# Revit family: 13961 Информационный указатель «Линк» Хоббика
name_source: partatom
category: Антураж
revit_build: Autodesk Revit 2018 (Build: 20180423_1000(x64)
units: mm (PartAtom-declared; Revit-internal decimal feet)

## family parameters
Всегда вертикально = Да
Источник визуального образа = Геометрия семейства
На основе рабочей плоскости = Нет
Общий = Нет
При загрузке вырезать с полостями = Нет
Точка расчета площади = Нет

## types (2) — shared parameters
URL = https://hobbyka.ru
Артикул товара = Арт. 13961
Высота = 2500 мм
Группа модели = Стенды и указатели
Длина = 1100 мм
Изготовитель = ООО «Хоббика»
Изображение типоразмера = Информационный указатель «Линк» Арт 13961.jpg
Материал изделия = Сталь, дерево
Цвет каркаса = Сталь
Цвет отделки = Дерево

## per-type parameters (varying)
| type | 3 стрелки | 4 стрелки | Описание | Ширина |
| 3 стрелки | Да | Нет | Информационный указатель «Линк». Версия 3 стрелки | 560 мм |
| 4 стрелки | Нет | Да | Информационный указатель «Линк». Версия 4 стрелки | 1000 мм |
